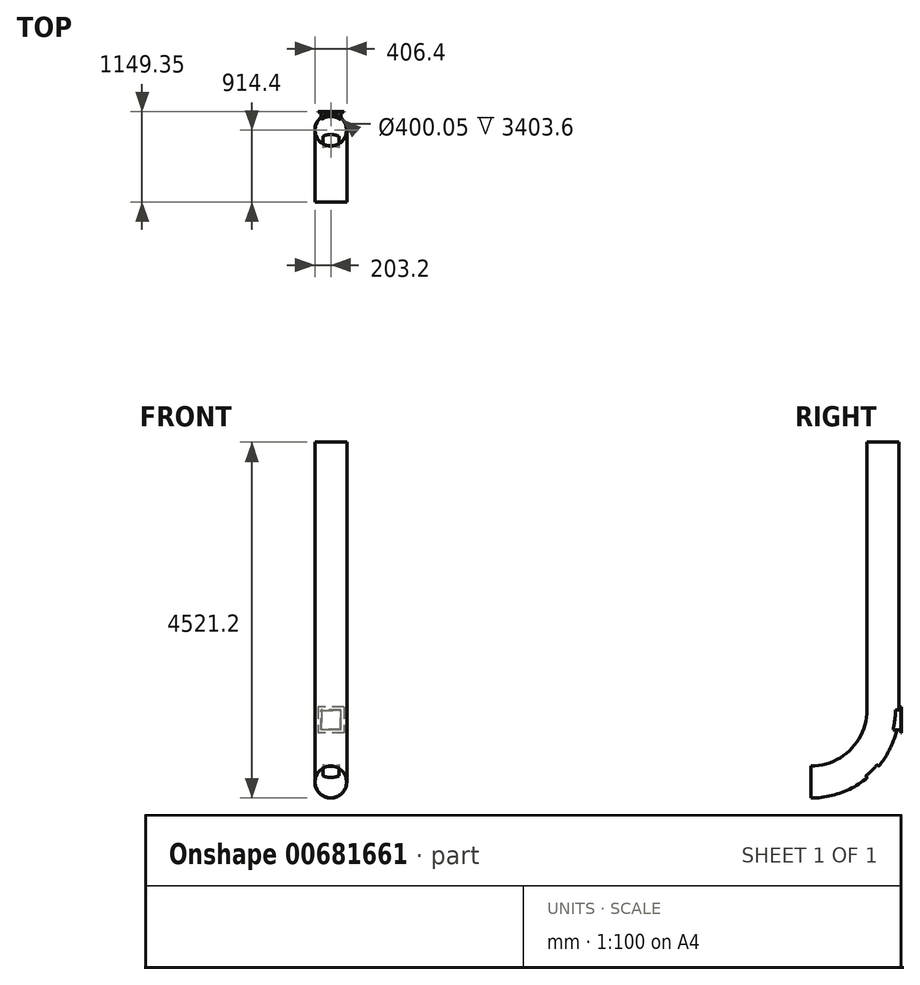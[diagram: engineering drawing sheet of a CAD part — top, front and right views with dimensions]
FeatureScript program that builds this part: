
annotation { "Feature Type Name" : "Feature", "Feature Type Description" : "" }
export const myFeature = defineFeature(function(context is Context, id is Id, definition is map)
    precondition{}
    {
        {
            var Q0;
            Q0=qCreatedBy(makeId("Right.planeOp"),FACE);
            var sketch = newSketch(context, id + "F0", { "sketchPlane" : qUnion([Q0])});
            skLineSegment(sketch, "E0", {"start": v(0, 0) * mm, "end": v(0, -3403.6) * mm, "construction": true});
            skLineSegment(sketch, "E1", {"start": v(0, -3403.6) * mm, "end": v(-914.4, -3403.6) * mm, "construction": true});
            skLineSegment(sketch, "E2", {"start": v(0, -3403.6) * mm, "end": v(0, -4318) * mm, "construction": true});
            skLineSegment(sketch, "E3", {"start": v(0, -4318) * mm, "end": v(-914.4, -4318) * mm, "construction": true});
            skLineSegment(sketch, "E4", {"start": v(-914.4, -4318) * mm, "end": v(-914.4, -3403.6) * mm, "construction": true});
            skSolve(sketch);
        }
        {
            var Q0;
            Q0=sQuery(id+"F0.wireOp",EDGE,"E1");
            cPlane(context, id + "F1", {"entities" : qUnion([Q0]), "cplaneType" : CPlaneType.LINE_ANGLE, "offset" : 25.4 * mm, "angle" : 0 * degree, "width" : 152.4 * mm, "height" : 152.4 * mm});
        }
        {
            var Q0;
            Q0=qCreatedBy(id+"F1.planeOp",FACE);
            var sketch = newSketch(context, id + "F2", { "sketchPlane" : qUnion([Q0])});
            skCircle(sketch, "E5", {"center": v(0, 0) * mm, "radius": 203.2 * mm});
            skCircle(sketch, "E6", {"center": v(0, 0) * mm, "radius": 200.03 * mm});
            skLineSegment(sketch, "E7", {"start": v(0, 914.4) * mm, "end": v(304.8, 914.4) * mm, "construction": true});
            skSolve(sketch);
        }
        {
            var Q0;
            Q0=makeQuery(id+"F2.imprint","IMPRINT",FACE,{"disambiguationData":[TD([[makeQuery(id+"F2.imprint","IMPRINT",EDGE,{"derivedFrom":sQuery(id+"F2.wireOp",EDGE,"E5")}),1.0]])]});
            var Q1;
            Q1=sQuery(id+"F2.wireOp",EDGE,"E5");
            var Q2;
            Q2=sQuery(id+"F2.wireOp",EDGE,"E7");
            revolve(context, id + "F3", {"surfaceOperationType" : NewSurfaceOperationType.NEW, "entities" : qUnion([Q0]), "surfaceEntities" : qUnion([Q1]), "axis" : qUnion([Q2]), "revolveType" : RevolveType.ONE_DIRECTION, "oppositeDirection" : true, "angle" : 90 * degree});
        }
        {
            var Q0;
            Q0=qCreatedBy(makeId("Top.planeOp"),FACE);
            var sketch = newSketch(context, id + "F4", { "sketchPlane" : qUnion([Q0])});
            skCircle(sketch, "E8", {"center": v(0, 0) * mm, "radius": 203.2 * mm});
            skCircle(sketch, "E9", {"center": v(0, 0) * mm, "radius": 200.03 * mm});
            skSolve(sketch);
        }
        {
            var Q0;
            Q0=makeQuery(id+"F4.imprint","IMPRINT",FACE,{"disambiguationData":[TD([[makeQuery(id+"F4.imprint","IMPRINT",EDGE,{"derivedFrom":sQuery(id+"F4.wireOp",EDGE,"E8")}),1.0]])]});
            var Q1;
            Q1=sQuery(id+"F4.wireOp",EDGE,"E8");
            extrude(context, id + "F5", {"entities" : qUnion([Q0]), "operationType" : NewBodyOperationType.ADD, "surfaceEntities" : qUnion([Q1]), "oppositeDirection" : true, "depth" : 3403.6 * mm, "offsetDistance" : 25.4 * mm});
        }
        {
            var Q0;
            Q0=sQuery(id+"F0.wireOp",EDGE,"E2");
            cPlane(context, id + "F6", {"entities" : qUnion([Q0]), "cplaneType" : CPlaneType.LINE_ANGLE, "offset" : 25.4 * mm, "angle" : 90 * degree, "width" : 152.4 * mm, "height" : 152.4 * mm});
        }
        {
            var Q0;
            Q0=qCreatedBy(id+"F6.planeOp",FACE);
            var sketch = newSketch(context, id + "F7", { "sketchPlane" : qUnion([Q0])});
            skLineSegment(sketch, "E10", {"start": v(0, -3530.65) * mm, "end": v(0, -3657.65) * mm});
            skLineSegment(sketch, "E11", {"start": v(0, -3657.65) * mm, "end": v(0, -3403.65) * mm});
            skLineSegment(sketch, "E12.bottom", {"start": v(-127, -3657.65) * mm, "end": v(127, -3657.65) * mm});
            skLineSegment(sketch, "E12.top", {"start": v(-127, -3403.65) * mm, "end": v(127, -3403.65) * mm});
            skLineSegment(sketch, "E12.left", {"start": v(-127, -3657.65) * mm, "end": v(-127, -3403.65) * mm});
            skLineSegment(sketch, "E12.right", {"start": v(127, -3657.65) * mm, "end": v(127, -3403.65) * mm});
            skPoint(sketch, "E12.middle", {"position": v(0, -3530.65) * mm});
            skLineSegment(sketch, "E13.bottom", {"start": v(-120.65, -3651.3) * mm, "end": v(120.65, -3651.3) * mm});
            skLineSegment(sketch, "E13.top", {"start": v(-120.65, -3410) * mm, "end": v(120.65, -3410) * mm});
            skLineSegment(sketch, "E13.left", {"start": v(-120.65, -3651.3) * mm, "end": v(-120.65, -3410) * mm});
            skLineSegment(sketch, "E13.right", {"start": v(120.65, -3651.3) * mm, "end": v(120.65, -3410) * mm});
            skLineSegment(sketch, "E14.bottom", {"start": v(-165.1, -3695.75) * mm, "end": v(165.1, -3695.75) * mm});
            skLineSegment(sketch, "E14.top", {"start": v(-165.1, -3365.55) * mm, "end": v(165.1, -3365.55) * mm});
            skLineSegment(sketch, "E14.left", {"start": v(-165.1, -3695.75) * mm, "end": v(-165.1, -3365.55) * mm});
            skLineSegment(sketch, "E14.right", {"start": v(165.1, -3695.75) * mm, "end": v(165.1, -3365.55) * mm});
            skSolve(sketch);
        }
        {
            var Q0;
            {var subQ0=sQuery(id+"F7.wireOp",EDGE,"E13.left");Q0=makeQuery(id+"F7.imprint","IMPRINT",FACE,{"disambiguationData":[TD([[makeQuery(id+"F7.imprint","IMPRINT",EDGE,{"derivedFrom":subQ0}),-1.0]])]});}
            var Q1;
            {var subQ0=sQuery(id+"F7.wireOp",EDGE,"E13.right");Q1=makeQuery(id+"F7.imprint","IMPRINT",FACE,{"disambiguationData":[TD([[makeQuery(id+"F7.imprint","IMPRINT",EDGE,{"derivedFrom":subQ0}),1.0]])]});}
            extrude(context, id + "F8", {"entities" : qUnion([Q0, Q1]), "operationType" : NewBodyOperationType.REMOVE, "depth" : 497.84 * mm, "offsetDistance" : 25.4 * mm});
        }
        {
            var Q0;
            {var subQ3=sQuery(id+"F7.wireOp",EDGE,"E12.right");Q0=makeQuery(id+"F7.imprint","IMPRINT",FACE,{"disambiguationData":[TD([[makeQuery(id+"F7.imprint","IMPRINT",EDGE,{"derivedFrom":subQ3}),1.0]])]});}
            var Q1;
            {var subQ3=sQuery(id+"F7.wireOp",EDGE,"E12.left");Q1=makeQuery(id+"F7.imprint","IMPRINT",FACE,{"disambiguationData":[TD([[makeQuery(id+"F7.imprint","IMPRINT",EDGE,{"derivedFrom":subQ3}),-1.0]])]});}
            extrude(context, id + "F9", {"entities" : qUnion([Q0, Q1]), "operationType" : NewBodyOperationType.ADD, "depth" : 228.6 * mm, "offsetDistance" : 25.4 * mm});
        }
        {
            var Q0;
            Q0=makeQuery(id+"F2.imprint","IMPRINT",FACE,{"disambiguationData":[TD([[makeQuery(id+"F2.imprint","IMPRINT",EDGE,{"derivedFrom":sQuery(id+"F2.wireOp",EDGE,"E6")}),1.0]])]});
            var Q1;
            Q1=sQuery(id+"F2.wireOp",EDGE,"E7");
            revolve(context, id + "F10", {"operationType" : NewBodyOperationType.REMOVE, "surfaceOperationType" : NewSurfaceOperationType.NEW, "entities" : qUnion([Q0]), "axis" : qUnion([Q1]), "revolveType" : RevolveType.ONE_DIRECTION, "oppositeDirection" : true, "angle" : 30 * degree});
        }
        {
            var Q0;
            Q0=makeQuery(id+"F9.opExtrude","CAP_FACE",FACE,{"disambiguationData":[OSD([sQuery(id+"F7.wireOp",EDGE,"E12.bottom"),sQuery(id+"F7.wireOp",EDGE,"E12.top"),sQuery(id+"F7.wireOp",EDGE,"E12.left"),sQuery(id+"F7.wireOp",EDGE,"E12.right"),sQuery(id+"F7.wireOp",EDGE,"E13.bottom"),sQuery(id+"F7.wireOp",EDGE,"E13.top"),sQuery(id+"F7.wireOp",EDGE,"E13.left"),sQuery(id+"F7.wireOp",EDGE,"E13.right")])],"isStart":false});
            cPlane(context, id + "F11", {"entities" : qUnion([Q0]), "cplaneType" : CPlaneType.OFFSET, "offset" : 0 * mm, "width" : 152.4 * mm, "height" : 152.4 * mm});
        }
        {
            var Q0;
            Q0=qCreatedBy(id+"F11.planeOp",FACE);
            var sketch = newSketch(context, id + "F12", { "sketchPlane" : qUnion([Q0])});
            skLineSegment(sketch, "E15.bottom", {"start": v(-120.65, -3410) * mm, "end": v(120.65, -3410) * mm});
            skLineSegment(sketch, "E15.top", {"start": v(-120.65, -3651.3) * mm, "end": v(120.65, -3651.3) * mm});
            skLineSegment(sketch, "E15.left", {"start": v(-120.65, -3410) * mm, "end": v(-120.65, -3651.3) * mm});
            skLineSegment(sketch, "E15.right", {"start": v(120.65, -3410) * mm, "end": v(120.65, -3651.3) * mm});
            skPoint(sketch, "E15.middle", {"position": v(0, -3530.65) * mm});
            skLineSegment(sketch, "E16.bottom", {"start": v(-165.1, -3365.55) * mm, "end": v(165.1, -3365.55) * mm});
            skLineSegment(sketch, "E16.top", {"start": v(-165.1, -3695.75) * mm, "end": v(165.1, -3695.75) * mm});
            skLineSegment(sketch, "E16.left", {"start": v(-165.1, -3365.55) * mm, "end": v(-165.1, -3695.75) * mm});
            skLineSegment(sketch, "E16.right", {"start": v(165.1, -3365.55) * mm, "end": v(165.1, -3695.75) * mm});
            skSolve(sketch);
        }
        {
            var Q0;
            Q0=makeQuery(id+"F12.imprint","IMPRINT",FACE,{"disambiguationData":[TD([[makeQuery(id+"F12.imprint","IMPRINT",EDGE,{"derivedFrom":sQuery(id+"F12.wireOp",EDGE,"E15.bottom")}),1.0]])]});
            extrude(context, id + "F13", {"entities" : qUnion([Q0]), "operationType" : NewBodyOperationType.ADD, "depth" : 6.35 * mm, "offsetDistance" : 25.4 * mm});
        }
        {
            var Q0;
            Q0=qCreatedBy(id+"F6.planeOp",FACE);
            var sketch = newSketch(context, id + "F14", { "sketchPlane" : qUnion([Q0])});
            skLineSegment(sketch, "E17", {"start": v(203.03, -4318) * mm, "end": v(-0.17, -4318) * mm, "construction": true});
            skSolve(sketch);
        }
        {
            var Q0;
            Q0=sQuery(id+"F14.wireOp",EDGE,"E17");
            cPlane(context, id + "F15", {"entities" : qUnion([Q0]), "cplaneType" : CPlaneType.LINE_ANGLE, "offset" : 25.4 * mm, "angle" : 135 * degree, "width" : 152.4 * mm, "height" : 152.4 * mm});
        }
        {
            var Q0;
            Q0=qCreatedBy(id+"F15.planeOp",FACE);
            var sketch = newSketch(context, id + "F16", { "sketchPlane" : qUnion([Q0])});
            skLineSegment(sketch, "E18.bottom", {"start": v(101.6, -3154.51) * mm, "end": v(-101.6, -3154.51) * mm});
            skLineSegment(sketch, "E18.top", {"start": v(101.6, -2951.31) * mm, "end": v(-101.6, -2951.31) * mm});
            skLineSegment(sketch, "E18.left", {"start": v(101.6, -3154.51) * mm, "end": v(101.6, -2951.31) * mm});
            skLineSegment(sketch, "E18.right", {"start": v(-101.6, -3154.51) * mm, "end": v(-101.6, -2951.31) * mm});
            skPoint(sketch, "E18.middle", {"position": v(0, -3052.91) * mm});
            skSolve(sketch);
        }
        {
            var Q0;
            Q0=makeQuery(id+"F16.imprint","IMPRINT",FACE,{"disambiguationData":[TD([[makeQuery(id+"F16.imprint","IMPRINT",EDGE,{"derivedFrom":sQuery(id+"F16.wireOp",EDGE,"E18.bottom")}),-1.0]])]});
            extrude(context, id + "F17", {"entities" : qUnion([Q0]), "operationType" : NewBodyOperationType.REMOVE, "depth" : 325.12 * mm, "offsetDistance" : 25.4 * mm});
        }
    });
